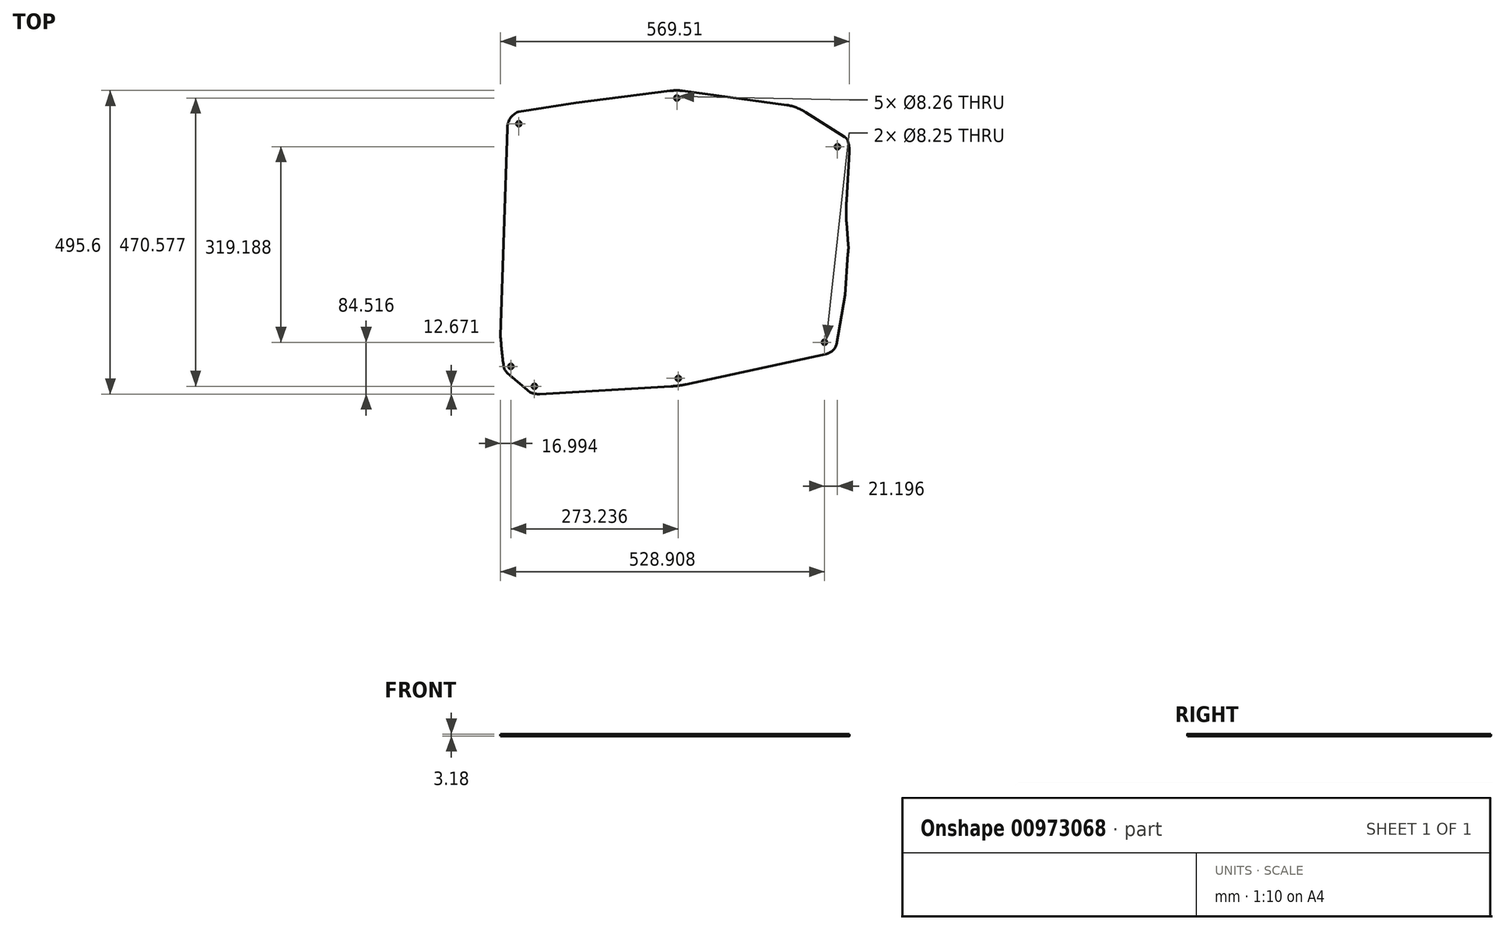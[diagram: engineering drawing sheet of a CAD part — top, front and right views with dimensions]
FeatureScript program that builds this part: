
annotation { "Feature Type Name" : "Feature", "Feature Type Description" : "" }
export const myFeature = defineFeature(function(context is Context, id is Id, definition is map)
    precondition{}
    {
        {
            var Q0;
            Q0=qCreatedBy(makeId("Top.planeOp"),FACE);
            var sketch = newSketch(context, id + "F0", { "sketchPlane" : qUnion([Q0])});
            skCircle(sketch, "E0", {"center": v(86.8, 59.7) * mm, "radius": 4.13 * mm});
            skCircle(sketch, "E1", {"center": v(125.26, 27.28) * mm, "radius": 4.13 * mm});
            skCircle(sketch, "E2", {"center": v(598.72, 99.13) * mm, "radius": 4.13 * mm});
            skCircle(sketch, "E3", {"center": v(360.04, 40.13) * mm, "radius": 4.13 * mm});
            skCircle(sketch, "E4", {"center": v(99.73, 455.78) * mm, "radius": 4.13 * mm});
            skCircle(sketch, "E5", {"center": v(357.75, 497.86) * mm, "radius": 4.13 * mm});
            skCircle(sketch, "E6", {"center": v(619.91, 418.31) * mm, "radius": 4.13 * mm});
            skPoint(sketch, "E7", {"position": v(636, 226.37) * mm});
            skPoint(sketch, "E8", {"position": v(73.47, 230.3) * mm});
            skLineSegment(sketch, "E9", {"start": v(118.22, 17.33) * mm, "end": v(81.14, 48.87) * mm});
            skLineSegment(sketch, "E10", {"start": v(69.81, 110.42) * mm, "end": v(80.9, 448.12) * mm});
            skLineSegment(sketch, "E11", {"start": v(99.4, 475.5) * mm, "end": v(192.75, 489.81) * mm});
            skLineSegment(sketch, "E12", {"start": v(192.75, 489.81) * mm, "end": v(346.48, 509.39) * mm});
            skLineSegment(sketch, "E13", {"start": v(366.6, 509.57) * mm, "end": v(537.37, 486.37) * mm});
            skLineSegment(sketch, "E14", {"start": v(567.64, 474.77) * mm, "end": v(631.64, 434.34) * mm});
            skLineSegment(sketch, "E15", {"start": v(639.25, 410.04) * mm, "end": v(634.9, 331.55) * mm});
            skLineSegment(sketch, "E16", {"start": v(634.72, 294.57) * mm, "end": v(637.62, 258.13) * mm});
            skLineSegment(sketch, "E17", {"start": v(636.9, 243.63) * mm, "end": v(632.54, 176.56) * mm});
            skLineSegment(sketch, "E18", {"start": v(632.54, 176.56) * mm, "end": v(618.4, 95.52) * mm});
            skLineSegment(sketch, "E19", {"start": v(601.36, 79.93) * mm, "end": v(372.77, 30.26) * mm});
            skLineSegment(sketch, "E20", {"start": v(347.93, 27.18) * mm, "end": v(133.65, 14.67) * mm});
            skArc(sketch, "E21", {"start": v(118.22, 17.33) * mm, "mid": v(125.78, 15.11) * mm, "end": v(133.65, 14.67) * mm});
            skArc(sketch, "E22", {"start": v(74.65, 63.3) * mm, "mid": v(76.27, 55.36) * mm, "end": v(81.14, 48.87) * mm});
            skArc(sketch, "E23", {"start": v(69.81, 110.42) * mm, "mid": v(71.83, 86.82) * mm, "end": v(74.65, 63.3) * mm});
            skArc(sketch, "E24", {"start": v(99.4, 475.5) * mm, "mid": v(85.78, 464.76) * mm, "end": v(80.9, 448.12) * mm});
            skArc(sketch, "E25", {"start": v(366.6, 509.57) * mm, "mid": v(356.53, 510.2) * mm, "end": v(346.48, 509.39) * mm});
            skArc(sketch, "E26", {"start": v(567.64, 474.77) * mm, "mid": v(553.08, 482.07) * mm, "end": v(537.37, 486.37) * mm});
            skArc(sketch, "E27", {"start": v(636.68, 427.94) * mm, "mid": v(634.7, 431.57) * mm, "end": v(631.64, 434.34) * mm});
            skArc(sketch, "E28", {"start": v(634.9, 331.55) * mm, "mid": v(634.03, 313.07) * mm, "end": v(634.72, 294.57) * mm});
            skArc(sketch, "E29", {"start": v(636.9, 243.63) * mm, "mid": v(637.73, 250.86) * mm, "end": v(637.62, 258.13) * mm});
            skArc(sketch, "E30", {"start": v(601.36, 79.93) * mm, "mid": v(611.99, 85.43) * mm, "end": v(618.4, 95.52) * mm});
            skArc(sketch, "E31", {"start": v(347.93, 27.18) * mm, "mid": v(360.4, 28.32) * mm, "end": v(372.77, 30.26) * mm});
            skPoint(sketch, "E32", {"position": v(379.49, 221.5) * mm});
            skPoint(sketch, "E33", {"position": v(300.7, 221.83) * mm});
            skPoint(sketch, "E34", {"position": v(300.7, 274.65) * mm});
            skArc(sketch, "E35", {"start": v(639.25, 410.04) * mm, "mid": v(638.85, 419.12) * mm, "end": v(636.68, 427.94) * mm});
            skSolve(sketch);
        }
        {
            var Q0;
            Q0=makeQuery(id+"F0.imprint","IMPRINT",FACE,{"disambiguationData":[TD([[makeQuery(id+"F0.imprint","IMPRINT",EDGE,{"derivedFrom":sQuery(id+"F0.wireOp",EDGE,"vKZH6yJm-D56Q-mBYb-3yTN-Bm9VfubhKv8t")}),1.0]])]});
            var Q1;
            Q1=makeQuery(id+"F0.imprint","IMPRINT",FACE,{"disambiguationData":[TD([[makeQuery(id+"F0.imprint","IMPRINT",EDGE,{"derivedFrom":sQuery(id+"F0.wireOp",EDGE,"E0")}),-1.0]])]});
            extrude(context, id + "F1", {"entities" : qUnion([Q0, Q1]), "depth" : 3.17 * mm, "offsetDistance" : 25.4 * mm});
        }
    });
